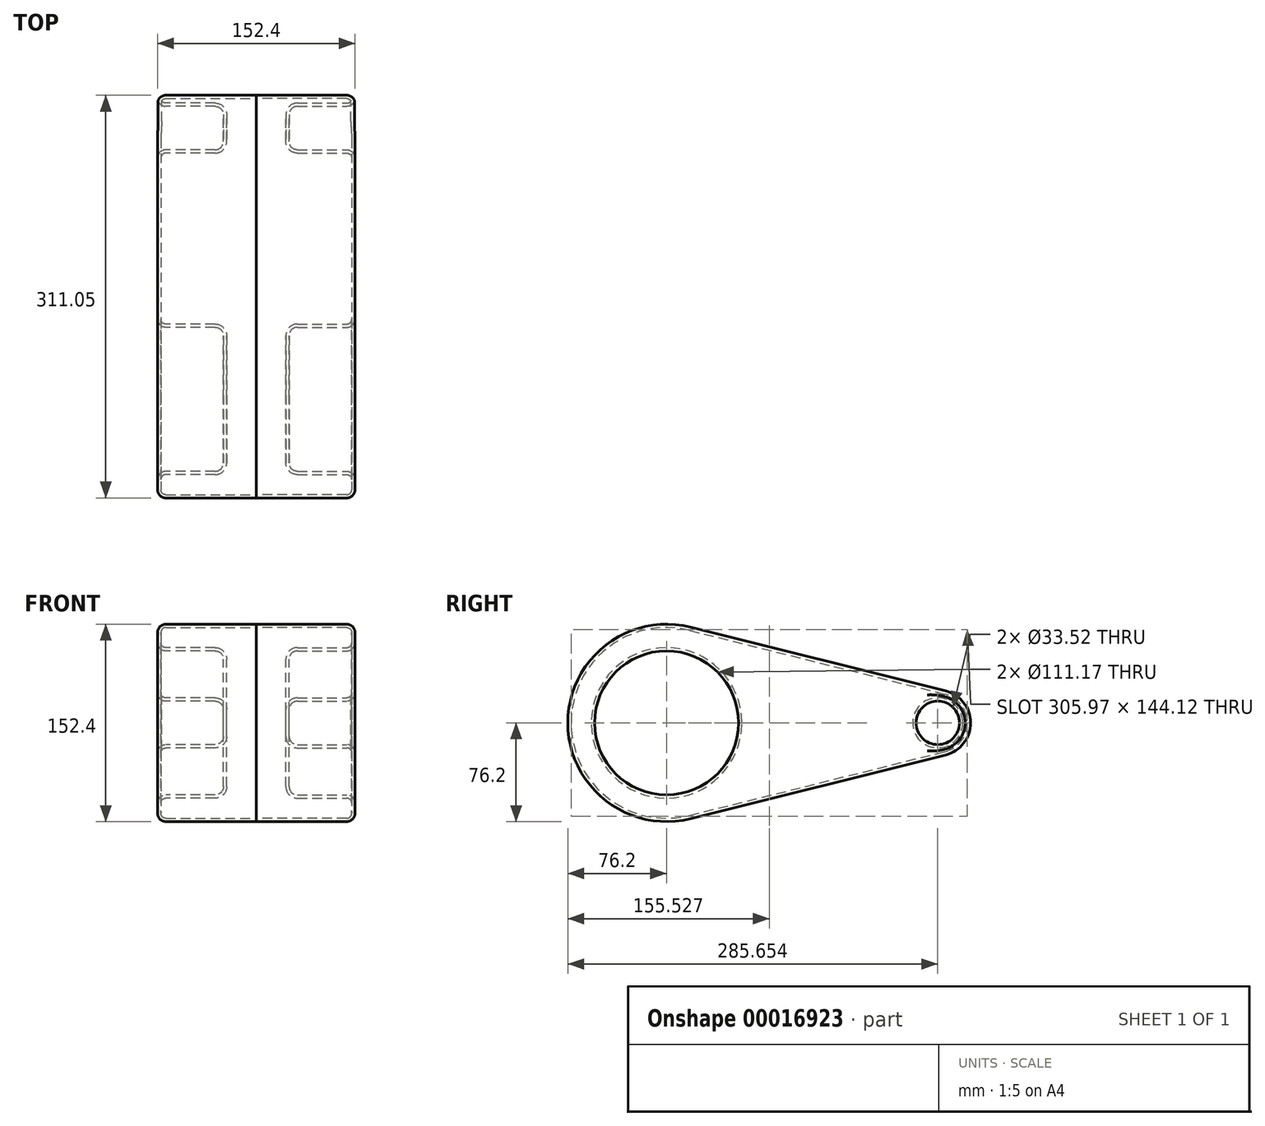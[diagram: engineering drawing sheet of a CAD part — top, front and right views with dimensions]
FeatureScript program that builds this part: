
annotation { "Feature Type Name" : "Feature", "Feature Type Description" : "" }
export const myFeature = defineFeature(function(context is Context, id is Id, definition is map)
    precondition{}
    {
        {
            var Q0;
            Q0=qCreatedBy(makeId("Right.planeOp"),FACE);
            var sketch = newSketch(context, id + "F0", { "sketchPlane" : qUnion([Q0])});
            skCircle(sketch, "E0", {"center": v(0, 0) * mm, "radius": 76.2 * mm});
            skCircle(sketch, "E1", {"center": v(209.45, 0) * mm, "radius": 25.4 * mm});
            skLineSegment(sketch, "E2", {"start": v(18.48, 73.92) * mm, "end": v(215.61, 24.64) * mm});
            skLineSegment(sketch, "E3", {"start": v(18.48, -73.92) * mm, "end": v(215.61, -24.64) * mm});
            skSolve(sketch);
        }
        {
            var Q0;
            {var subQ1=sQuery(id+"F0.wireOp",EDGE,"E2");Q0=makeQuery(id+"F0.imprint","IMPRINT",FACE,{"disambiguationData":[TD([[makeQuery(id+"F0.imprint","IMPRINT",EDGE,{"derivedFrom":subQ1}),-1.0]])]});}
            var Q1;
            {var subQ0=sQuery(id+"F0.wireOp",EDGE,"E0");var subQ2=makeQuery(id+"F0.imprint","INTERSECT",VERTEX,{"derivedFrom":[subQ0,sQuery(id+"F0.wireOp",EDGE,"E2")]});Q1=makeQuery(id+"F0.imprint","IMPRINT",FACE,{"disambiguationData":[TD([[makeQuery(id+"F0.imprint","IMPRINT",EDGE,{"disambiguationData":[TD([[subQ2,-1.0]])],"derivedFrom":subQ0}),1.0]])]});}
            var Q2;
            {var subQ0=sQuery(id+"F0.wireOp",EDGE,"E1");var subQ2=makeQuery(id+"F0.imprint","INTERSECT",VERTEX,{"derivedFrom":[subQ0,sQuery(id+"F0.wireOp",EDGE,"E2")]});Q2=makeQuery(id+"F0.imprint","IMPRINT",FACE,{"disambiguationData":[TD([[makeQuery(id+"F0.imprint","IMPRINT",EDGE,{"disambiguationData":[TD([[subQ2,-1.0]])],"derivedFrom":subQ0}),1.0]])]});}
            extrude(context, id + "F1", {"entities" : qUnion([Q0, Q1, Q2]), "depth" : 76.2 * mm});
        }
        {
            var Q0;
            Q0=makeQuery(id+"F1.opExtrude","CAP_FACE",FACE,{"disambiguationData":[OSD([sQuery(id+"F0.wireOp",EDGE,"E0"),sQuery(id+"F0.wireOp",EDGE,"E1"),sQuery(id+"F0.wireOp",EDGE,"E2"),sQuery(id+"F0.wireOp",EDGE,"E3")])],"isStart":false});
            var sketch = newSketch(context, id + "F2", { "sketchPlane" : qUnion([Q0])});
            skCircle(sketch, "E4", {"center": v(0, 0) * mm, "radius": 55.59 * mm});
            skCircle(sketch, "E5", {"center": v(209.45, 0) * mm, "radius": 16.76 * mm});
            skSolve(sketch);
        }
        {
            var Q0;
            Q0=makeQuery(id+"F2.imprint","IMPRINT",FACE,{"disambiguationData":[TD([[makeQuery(id+"F2.imprint","IMPRINT",EDGE,{"derivedFrom":sQuery(id+"F2.wireOp",EDGE,"E4")}),1.0]])]});
            var Q1;
            Q1=makeQuery(id+"F2.imprint","IMPRINT",FACE,{"disambiguationData":[TD([[makeQuery(id+"F2.imprint","IMPRINT",EDGE,{"derivedFrom":sQuery(id+"F2.wireOp",EDGE,"E5")}),1.0]])]});
            extrude(context, id + "F3", {"entities" : qUnion([Q0, Q1]), "operationType" : NewBodyOperationType.REMOVE, "oppositeDirection" : true, "depth" : 50.8 * mm});
        }
        {
            var Q0;
            Q0=makeQuery(id+"F1.opExtrude","CAP_FACE",FACE,{"disambiguationData":[OSD([sQuery(id+"F0.wireOp",EDGE,"E0"),sQuery(id+"F0.wireOp",EDGE,"E1"),sQuery(id+"F0.wireOp",EDGE,"E2"),sQuery(id+"F0.wireOp",EDGE,"E3")])],"isStart":false});
            var Q1;
            Q1=makeQuery(id+"F3.boolean.opBoolean","COPY",EDGE,{"derivedFrom":makeQuery(id+"F3.opExtrude","CAP_EDGE",EDGE,{"disambiguationData":[OSD([sQuery(id+"F2.wireOp",EDGE,"E4")])],"isStart":false})});
            var Q2;
            Q2=makeQuery(id+"F3.boolean.opBoolean","COPY",EDGE,{"derivedFrom":makeQuery(id+"F3.opExtrude","CAP_EDGE",EDGE,{"disambiguationData":[OSD([sQuery(id+"F2.wireOp",EDGE,"E5")])],"isStart":false})});
            fillet(context, id + "F4", {"entities" : qUnion([Q0, Q1, Q2]), "radius" : 6.35 * mm, "allowEdgeOverflow" : false});
        }
        {
            var Q0;
            Q0=makeQuery(id+"F1.opExtrude","CAP_FACE",FACE,{"disambiguationData":[OSD([sQuery(id+"F0.wireOp",EDGE,"E0"),sQuery(id+"F0.wireOp",EDGE,"E1"),sQuery(id+"F0.wireOp",EDGE,"E2"),sQuery(id+"F0.wireOp",EDGE,"E3")])],"isStart":true});
            shell(context, id + "F5", {"entities" : qUnion([Q0]), "thickness" : 2.54 * mm});
        }
        {
            var Q0;
            Q0=makeQuery(id+"F1.opExtrude","SWEPT_BODY",BODY,{"disambiguationData":[OSD([sQuery(id+"F0.wireOp",EDGE,"E0"),sQuery(id+"F0.wireOp",EDGE,"E1"),sQuery(id+"F0.wireOp",EDGE,"E2"),sQuery(id+"F0.wireOp",EDGE,"E3")])]});
            var Q1;
            Q1=qCreatedBy(makeId("Right.planeOp"),FACE);
            mirror(context, id + "F6", {"entities" : qUnion([Q0]), "mirrorPlane" : qUnion([Q1])});
        }
    });
